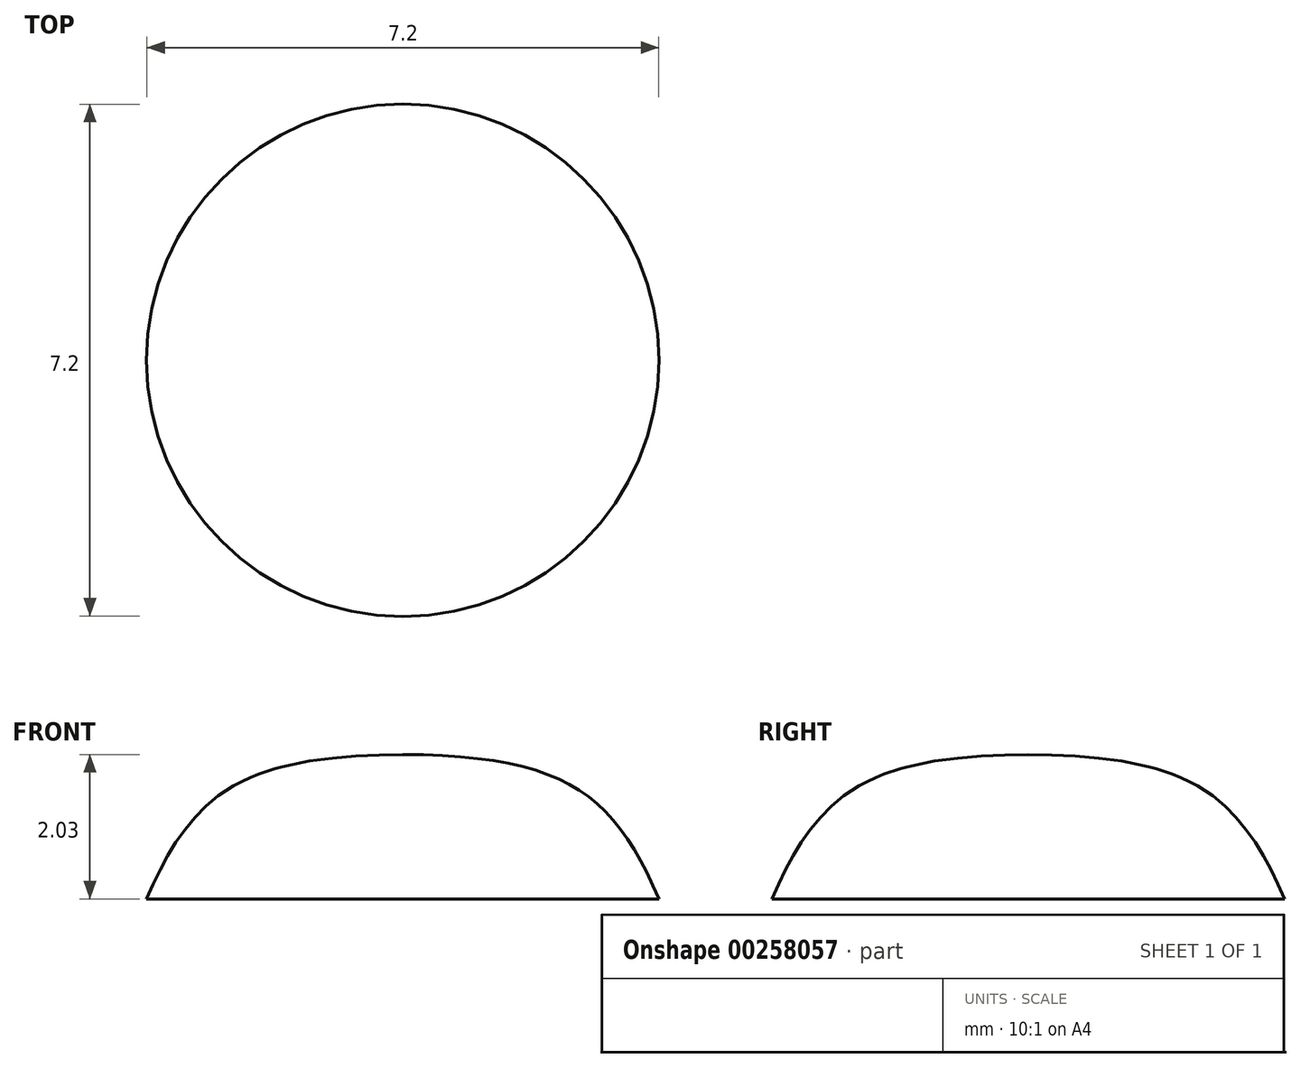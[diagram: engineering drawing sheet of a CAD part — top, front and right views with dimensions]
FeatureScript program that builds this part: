
annotation { "Feature Type Name" : "Feature", "Feature Type Description" : "" }
export const myFeature = defineFeature(function(context is Context, id is Id, definition is map)
    precondition{}
    {
        {
            var Q0;
            Q0=qCreatedBy(makeId("Front.planeOp"),FACE);
            var sketch = newSketch(context, id + "F0", { "sketchPlane" : qUnion([Q0])});
            skLineSegment(sketch, "E0", {"start": v(0, 3.2) * mm, "end": v(0, -3.16) * mm, "construction": true});
            skLineSegment(sketch, "E1.bottom", {"start": v(-0.76, 5.13) * mm, "end": v(0.76, 5.13) * mm});
            skLineSegment(sketch, "E1.top", {"start": v(-0.76, -3.25) * mm, "end": v(0.76, -3.25) * mm});
            skLineSegment(sketch, "E1.left", {"start": v(-0.76, 5.13) * mm, "end": v(-0.76, -3.25) * mm});
            skLineSegment(sketch, "E1.right", {"start": v(0.76, 5.13) * mm, "end": v(0.76, -3.25) * mm});
            skSolve(sketch);
        }
        {
            var Q0;
            Q0=sQuery(id+"F0.wireOp",EDGE,"E0");
            var Q1;
            Q1=sQuery(id+"F0.wireOp",EDGE,"E1.right");
            var Q2;
            Q2=sQuery(id+"F0.wireOp",EDGE,"E0");
            revolve(context, id + "F1", {"bodyType" : ToolBodyType.SURFACE, "surfaceEntities" : qUnion([Q0, Q1]), "axis" : qUnion([Q2]), "revolveType" : RevolveType.FULL});
        }
        {
            var Q0;
            Q0=qCreatedBy(makeId("Front.planeOp"),FACE);
            var sketch = newSketch(context, id + "F2", { "sketchPlane" : qUnion([Q0])});
            skLineSegment(sketch, "E2", {"start": v(0, 11.25) * mm, "end": v(0, 9.22) * mm});
            skLineSegment(sketch, "E3", {"start": v(0, 5.13) * mm, "end": v(0, 3.1) * mm});
            skLineSegment(sketch, "E4", {"start": v(0, 3.1) * mm, "end": v(3.6, 3.1) * mm});
            skFitSpline(sketch, "E5", {"points": [v(0, 5.13) * mm, v(3.6, 3.1) * mm], "startDerivative": vector(6.85, -0.06) * mm, "endDerivative": vector(1.96, -4.5) * mm});
            skSolve(sketch);
        }
        {
            var Q0;
            Q0=makeQuery(id+"F2.imprint","IMPRINT",FACE,{"disambiguationData":[TD([[makeQuery(id+"F2.imprint","IMPRINT",EDGE,{"derivedFrom":sQuery(id+"F2.wireOp",EDGE,"E3")}),1.0]])]});
            var Q1;
            Q1=sQuery(id+"F2.wireOp",EDGE,"E3");
            revolve(context, id + "F3", {"entities" : qUnion([Q0]), "axis" : qUnion([Q1]), "revolveType" : RevolveType.FULL});
        }
    });
